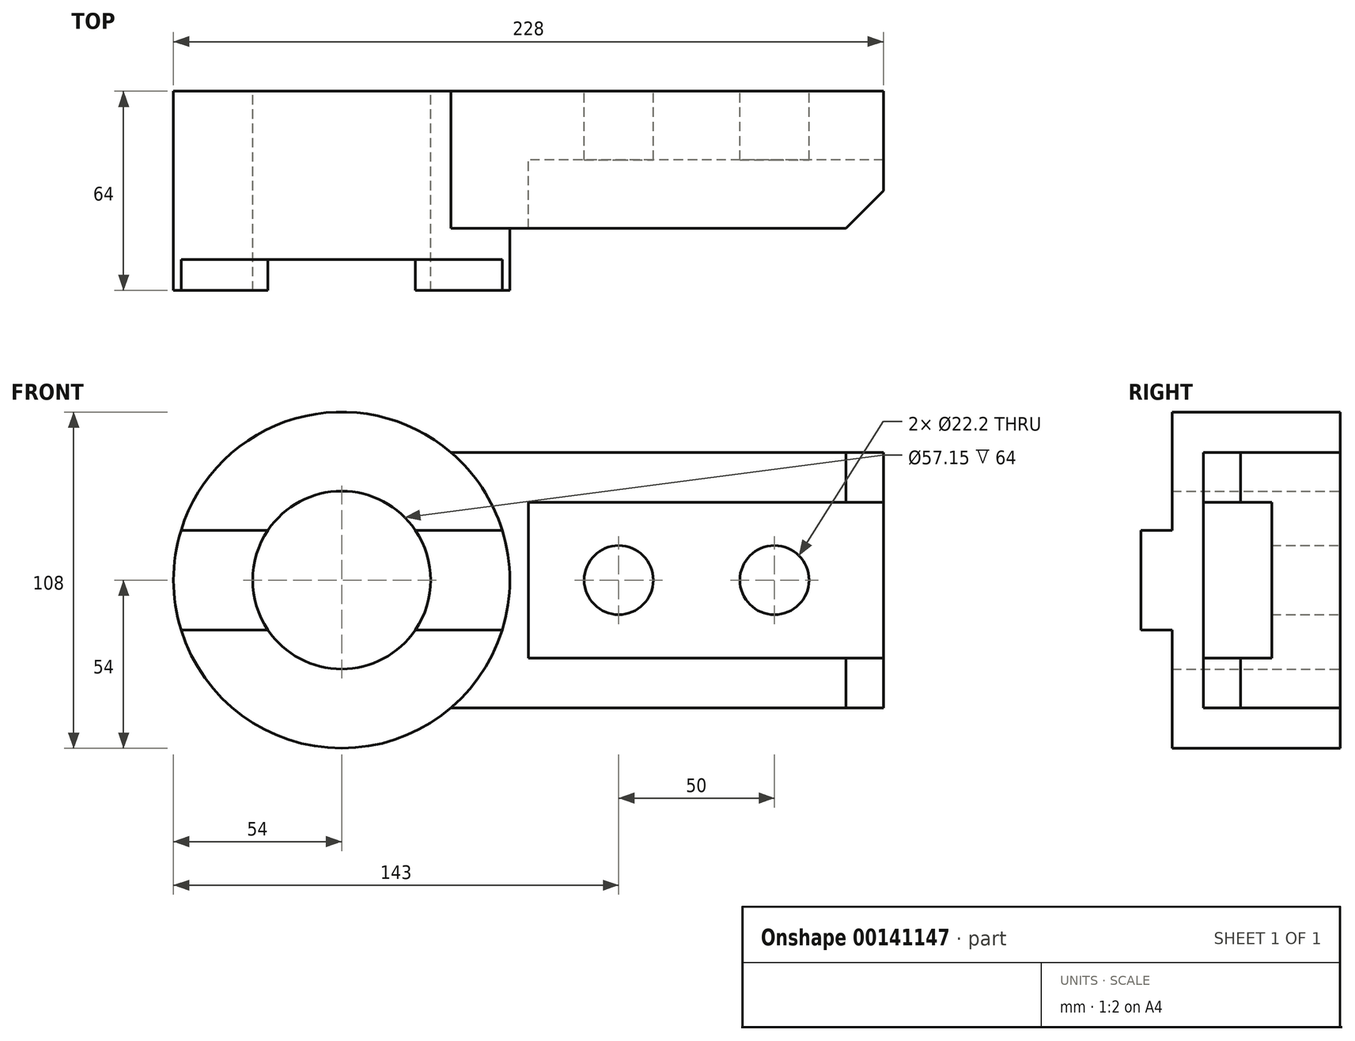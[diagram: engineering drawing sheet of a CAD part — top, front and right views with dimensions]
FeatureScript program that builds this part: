
annotation { "Feature Type Name" : "Feature", "Feature Type Description" : "" }
export const myFeature = defineFeature(function(context is Context, id is Id, definition is map)
    precondition{}
    {
        {
            var Q0;
            Q0=qCreatedBy(makeId("Front.planeOp"),FACE);
            var sketch = newSketch(context, id + "F0", { "sketchPlane" : qUnion([Q0])});
            skCircle(sketch, "E0", {"center": v(0, 0) * mm, "radius": 28.58 * mm});
            skCircle(sketch, "E1", {"center": v(0, 0) * mm, "radius": 54 * mm});
            skLineSegment(sketch, "E2", {"start": v(-23.68, 16) * mm, "end": v(-51.58, 16) * mm});
            skLineSegment(sketch, "E3", {"start": v(-23.68, -16) * mm, "end": v(-51.58, -16) * mm});
            skLineSegment(sketch, "E4.MirrorCS", {"start": v(23.68, 16) * mm, "end": v(51.58, 16) * mm});
            skLineSegment(sketch, "E5.MirrorCS", {"start": v(23.68, -16) * mm, "end": v(51.58, -16) * mm});
            skLineSegment(sketch, "E6", {"start": v(35.14, 41) * mm, "end": v(174, 41) * mm});
            skLineSegment(sketch, "E7", {"start": v(174, 41) * mm, "end": v(174, 0) * mm});
            skLineSegment(sketch, "E8.MirrorCS", {"start": v(35.14, -41) * mm, "end": v(174, -41) * mm});
            skLineSegment(sketch, "E9.MirrorCS", {"start": v(174, -41) * mm, "end": v(174, 0) * mm});
            skLineSegment(sketch, "E10.bottom", {"start": v(174, 25) * mm, "end": v(60, 25) * mm});
            skLineSegment(sketch, "E10.top", {"start": v(174, -25) * mm, "end": v(60, -25) * mm});
            skLineSegment(sketch, "E10.left", {"start": v(174, 25) * mm, "end": v(174, -25) * mm});
            skLineSegment(sketch, "E10.right", {"start": v(60, 25) * mm, "end": v(60, -25) * mm});
            skCircle(sketch, "E11", {"center": v(89, 0) * mm, "radius": 11.1 * mm});
            skCircle(sketch, "E12", {"center": v(139, 0) * mm, "radius": 11.1 * mm});
            skSolve(sketch);
        }
        {
            var Q0;
            {var subQ0=sQuery(id+"F0.wireOp",EDGE,"E6");Q0=makeQuery(id+"F0.imprint","IMPRINT",FACE,{"disambiguationData":[TD([[makeQuery(id+"F0.imprint","IMPRINT",EDGE,{"derivedFrom":subQ0}),-1.0]])]});}
            extrude(context, id + "F1", {"entities" : qUnion([Q0]), "depth" : 44 * mm});
        }
        {
            var Q0;
            {var subQ1=sQuery(id+"F0.wireOp",EDGE,"E10.bottom");Q0=makeQuery(id+"F0.imprint","IMPRINT",FACE,{"disambiguationData":[TD([[makeQuery(id+"F0.imprint","IMPRINT",EDGE,{"derivedFrom":subQ1}),1.0]])]});}
            extrude(context, id + "F2", {"entities" : qUnion([Q0]), "operationType" : NewBodyOperationType.ADD, "depth" : 22 * mm});
        }
        {
            var Q0;
            {var subQ0=sQuery(id+"F0.wireOp",EDGE,"E2");Q0=makeQuery(id+"F0.imprint","IMPRINT",FACE,{"disambiguationData":[TD([[makeQuery(id+"F0.imprint","IMPRINT",EDGE,{"derivedFrom":subQ0}),1.0]])]});}
            var Q1;
            {var subQ0=sQuery(id+"F0.wireOp",EDGE,"E4.MirrorCS");Q1=makeQuery(id+"F0.imprint","IMPRINT",FACE,{"disambiguationData":[TD([[makeQuery(id+"F0.imprint","IMPRINT",EDGE,{"derivedFrom":subQ0}),-1.0]])]});}
            extrude(context, id + "F3", {"entities" : qUnion([Q0, Q1]), "operationType" : NewBodyOperationType.ADD, "depth" : 64 * mm});
        }
        {
            var Q0;
            {var subQ0=sQuery(id+"F0.wireOp",EDGE,"E2");Q0=makeQuery(id+"F0.imprint","IMPRINT",FACE,{"disambiguationData":[TD([[makeQuery(id+"F0.imprint","IMPRINT",EDGE,{"derivedFrom":subQ0}),-1.0]])]});}
            var Q1;
            {var subQ0=sQuery(id+"F0.wireOp",EDGE,"E3");Q1=makeQuery(id+"F0.imprint","IMPRINT",FACE,{"disambiguationData":[TD([[makeQuery(id+"F0.imprint","IMPRINT",EDGE,{"derivedFrom":subQ0}),1.0]])]});}
            extrude(context, id + "F4", {"entities" : qUnion([Q0, Q1]), "operationType" : NewBodyOperationType.ADD, "depth" : 54 * mm});
        }
        {
            var Q0;
            Q0=makeQuery(id+"F1.opExtrude","CAP_EDGE",EDGE,{"disambiguationData":[OSD([sQuery(id+"F0.wireOp",EDGE,"E9.MirrorCS")])],"isStart":false});
            var Q1;
            Q1=makeQuery(id+"F1.opExtrude","CAP_EDGE",EDGE,{"disambiguationData":[OSD([sQuery(id+"F0.wireOp",EDGE,"E7")])],"isStart":false});
            chamfer(context, id + "F5", {"entities" : qUnion([Q0, Q1]), "width" : 12 * mm, "tangentPropagation" : true});
        }
    });
